# Revit family: xled_pro_wide_xl_010065
name_source: partatom
category: Leuchten
revit_build: Autodesk Revit 2016 (Build: 20190508_0715(x64)
units: mm (PartAtom-declared; Revit-internal decimal feet)

## family parameters
Basisbauteil = Fläche
Beim Laden mit Abzugskörper schneiden = Nein
Bemaßung runder Anschluss = Durchmesser verwenden
Gemeinsam genutzt = Nein
Lichtquelle = Nein
Raumberechnungspunkt = Nein
Teiletyp = Normal

## types (1)
- XLED PRO Wide XL (1 x , 4400 lm, 4000 K)
    Beschreibung = Dimensions (L x W x H): 126 x 265 x 188 mm; Mains power supply: 220 – 240 V / 50 – 60 Hz; Mounting height max.: 6,00 m; Sensor Technology: passive infrared; Output: 48 W; Interconnection: Yes; Type of interconnection: Sensor/slave; Interconnection, number: maximum of 10 floodlights; Luminous flux: 4400 lm; Colour temperature: 4000 K; Colour variation LED: SDCM3; Colour Rendering Index CRI: 80-89; With lamp: Yes, STEINEL LED system; Lamp: LED cannot be replaced; LED life expectancy (max. °C): 50000 h; Drop in luminous flux in accordance with LM80: L70B10; LED cooling system: Passive Thermo Control; With motion detector: Yes; Detection angle: 240 °; Angle of aperture: 180 °; Sneak-by guard: Yes; Capability of masking out individual segments: Yes; Reach, radial: r = 5 m (52 m²); Reach, tangential: r = 12 m (302 m²); Photo-cell controller: Yes; Twilight setting: 2 – 1000 lx; Time setting: 5 sec – 15 min; Basic light level function: Yes; Basic light level function time: 10 min, all night; Soft light start: No; Continuous light: selectable, 4h; Impact resistance: IK03; IP-rating: IP54; Protection class: I; Ambient temperature: -20 – 40 °C; Housing material: Aluminium; Cover material: Plastic, transparent; Manufacturer's Warranty: 5 years; PU1, net weight: 1,841 kg; Version: black; PU1, EAN: 4007841010065
    CIE Flux Codes = 47 82 96 99 103
    Color Rendering = 80-89
    Color Temperature = 4000 K
    Frequency = 60 Hz, 50 Hz
    Height = 188 mm  [stored 0.616798 ft]
    Hersteller = Steinel
    Lamp Light Flux = 4400 lm
    Lamp count = 1
    Lampe = 1 x
    Length = 126 mm
    Luminous efficacy = 94 lm/W
    ModVariant = Nein
    Modell = 010065
    Mounting Type = Surface mounted
    Number of Poles = 1
    OnlyDefault = Ja
    Power Factor = 1
    Product Name = XLED PRO Wide XL
    Product group = Sensor-switched indoor light
    ProductGroupID = 30
    Protection Class = Protection class I
    Protection Degree = IP 54
    RlxData = <blob elided: 124005 chars, md5=5c7b9b77>
    Scheinlast = 48 VA
    Socket = socket
    Standby Power = 0 W
    System Light Flux = 4527 lm
    System Power = 48 W
    Typenbild = produkt1_010065.jpg
    Typenkommentare = Product without accessories
    URL = http://relux.com
    VarID = ---
    Voltage = 0 V
    Vorgabe-Ansicht = 1800 mm
    Weight = 0.00 kg
    Width = 265 mm

note: [stored X ft] marks values corroborated as IEEE doubles in the binary element streams (Revit-internal decimal feet)

## geometry (parser evidence)
native form markers: Blend x4, Sweep x14
no freeform markers — native parametric forms only
